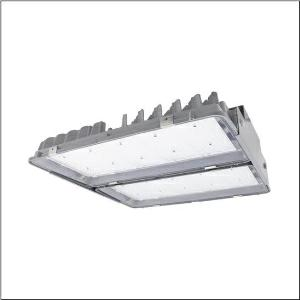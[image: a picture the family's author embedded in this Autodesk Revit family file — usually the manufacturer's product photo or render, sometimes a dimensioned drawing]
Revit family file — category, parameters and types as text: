
# Revit family: highbay_11xtreme_51hf61db4qma
name_source: partatom
category: Lighting Fixtures
units: mm (PartAtom-declared; Revit-internal decimal feet)

## family parameters
Cut with Voids When Loaded = No
Host = Face
Light Source = No
Part Type = Normal
Room Calculation Point = No
Round Connector Dimension = Use Diameter
Shared = No

## types (1)
- --- (1 x LED, 37300 lm, 193.8 W, 4000K)
    Apparent Load = 194 VA
    CIE Flux Codes = 88 96 99 100 100
    Color Rendering = 80
    Color Temperature = 4000K
    Default Elevation = 1800 mm
    Description = Highbay 11Xtreme, LED high bay luminaire, primary light control with lens, of PMMA, primary optical cover: cover, of toughened safety glass, light emission: direct distribution, primary light characteristic: symmetric, installation type: suspended mounting, surface-mounted, 2x LED module,for 1x 2x LED, rated luminous flux: 36.000lm, luminous efficacy: 178lm/W, light colour: 840, colour temperature: 4000K, with cable H07RN-F 5x 1.5mm², mains connection: 220..240V, AC, 50/60Hz, cable length: 1,5m, rated input power: 202W, luminaire housing, of diecast aluminium, coated, silver, length: 595mm, width: 560mm, height: 195mm, protection rating (complete): IP66, insulation class (complete): insulation class I (protective earthing), certification: CE, ENEC, UKCA, protection symbol: D, ball protection: ball impact resistant according to DIN VDE 0710 part 13 (with chain suspension), impact resistance: IK08, permissible operating ambient temperature: -25..+70°C, reducing of maximum allowable ambient temperature of 5°C with ceiling mounting, packaging unit: 1 piece
    Height = 157 mm
    Lamp = 1 x LED
    Lamp Light Flux = 37300 lm
    Lamp Power = 193.8 W
    Lamp count = 1
    Length = 593 mm
    Luminous efficacy = 192 lm/W
    Manufacturer = Siteco
    ModVariant = No
    Model = 51HF61DB4QMA
    Mounting Place = Ceiling
    Mounting Type = Pendant
    Number of Poles = 1
    OnlyDefault = Yes
    Power Factor = 1
    Product Name = Highbay 11Xtreme
    Product group = LED high bay luminaire
    ProductGroupID = 903
    Protection Class = Protection class I
    Protection Degree = IP 66
    RLX_Detail_Level = 1
    RLX_Emergency_Light_Flux = 0 lm
    RLX_Emergency_Type = 0
    RLX_Emergency_Type_DB = No
    RlxData = <blob elided: 33765 chars, md5=d4866192>
    Socket = socket
    Standby Power = 0 W
    System Light Flux = 37301 lm
    System Power = 194 W
    Type Comments = factory setting: luminous flux: 100 % | dim-lin: 254 | 648 mA
    Type Image = l_1258340.jpg
    URL = http://relux.com
    VarID = @adj_035839
    Voltage = 0 V
    Weight = 0.00 kg
    Width = 278 mm

## geometry (parser evidence)
native form markers: Blend x4, Sweep x10
no freeform markers — native parametric forms only
